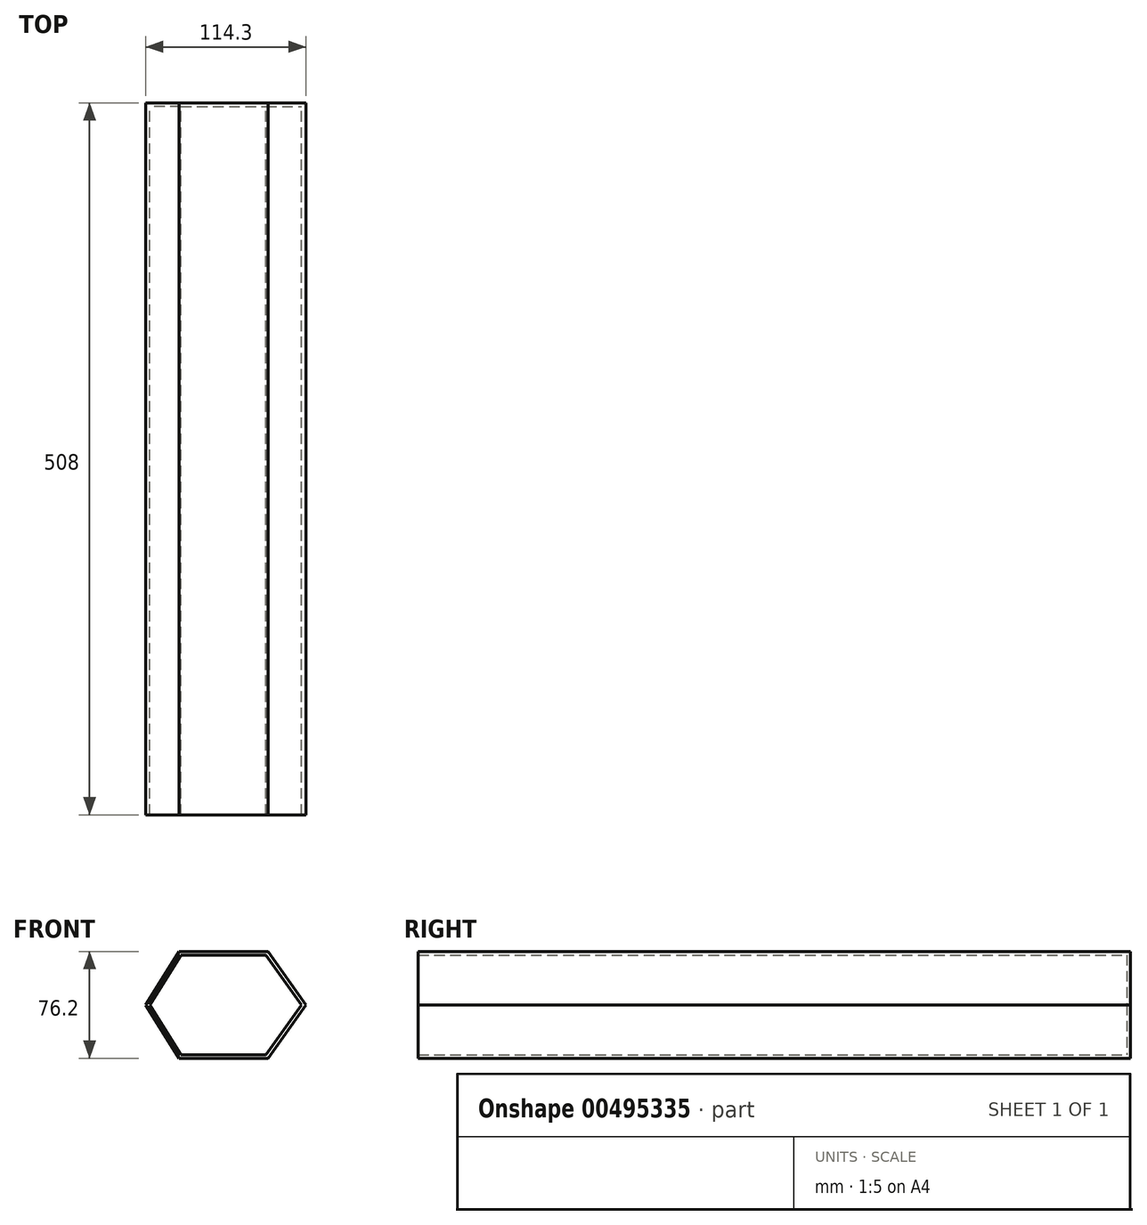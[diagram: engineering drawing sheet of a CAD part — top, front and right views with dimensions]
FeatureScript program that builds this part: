
annotation { "Feature Type Name" : "Feature", "Feature Type Description" : "" }
export const myFeature = defineFeature(function(context is Context, id is Id, definition is map)
    precondition{}
    {
        {
            var Q0;
            Q0=qCreatedBy(makeId("Front.planeOp"),FACE);
            var sketch = newSketch(context, id + "F0", { "sketchPlane" : qUnion([Q0])});
            skPoint(sketch, "E0", {"position": v(-63.5, 0) * mm});
            skPoint(sketch, "E1", {"position": v(50.8, 0) * mm});
            skPoint(sketch, "E2", {"position": v(-39.82, -38.1) * mm});
            skPoint(sketch, "E3", {"position": v(23.68, -38.1) * mm});
            skPoint(sketch, "E4", {"position": v(23.68, 38.1) * mm});
            skPoint(sketch, "E5", {"position": v(-39.82, 38.1) * mm});
            skLineSegment(sketch, "E6", {"start": v(-39.82, 38.1) * mm, "end": v(23.68, 38.1) * mm});
            skLineSegment(sketch, "E7", {"start": v(-39.82, -38.1) * mm, "end": v(23.68, -38.1) * mm});
            skLineSegment(sketch, "E8", {"start": v(50.8, 0) * mm, "end": v(23.68, 38.1) * mm});
            skLineSegment(sketch, "E9", {"start": v(-39.82, 38.1) * mm, "end": v(-63.5, 0) * mm});
            skLineSegment(sketch, "E10", {"start": v(-63.5, 0) * mm, "end": v(-39.82, -38.1) * mm});
            skLineSegment(sketch, "E11", {"start": v(23.68, -38.1) * mm, "end": v(50.8, 0) * mm});
            skSolve(sketch);
        }
        {
            var Q0;
            Q0=makeQuery(id+"F0.imprint","IMPRINT",FACE,{"disambiguationData":[TD([[makeQuery(id+"F0.imprint","IMPRINT",EDGE,{"derivedFrom":sQuery(id+"F0.wireOp",EDGE,"E6")}),-1.0]])]});
            extrude(context, id + "F1", {"entities" : qUnion([Q0]), "endBound" : BoundingType.SYMMETRIC, "depth" : 508 * mm});
        }
        {
            var Q0;
            Q0=makeQuery(id+"F1.opExtrude","CAP_FACE",FACE,{"disambiguationData":[OSD([sQuery(id+"F0.wireOp",EDGE,"E6"),sQuery(id+"F0.wireOp",EDGE,"E7"),sQuery(id+"F0.wireOp",EDGE,"E8"),sQuery(id+"F0.wireOp",EDGE,"E9"),sQuery(id+"F0.wireOp",EDGE,"E10"),sQuery(id+"F0.wireOp",EDGE,"E11")])],"isStart":false});
            shell(context, id + "F2", {"entities" : qUnion([Q0]), "thickness" : 2.54 * mm});
        }
    });
